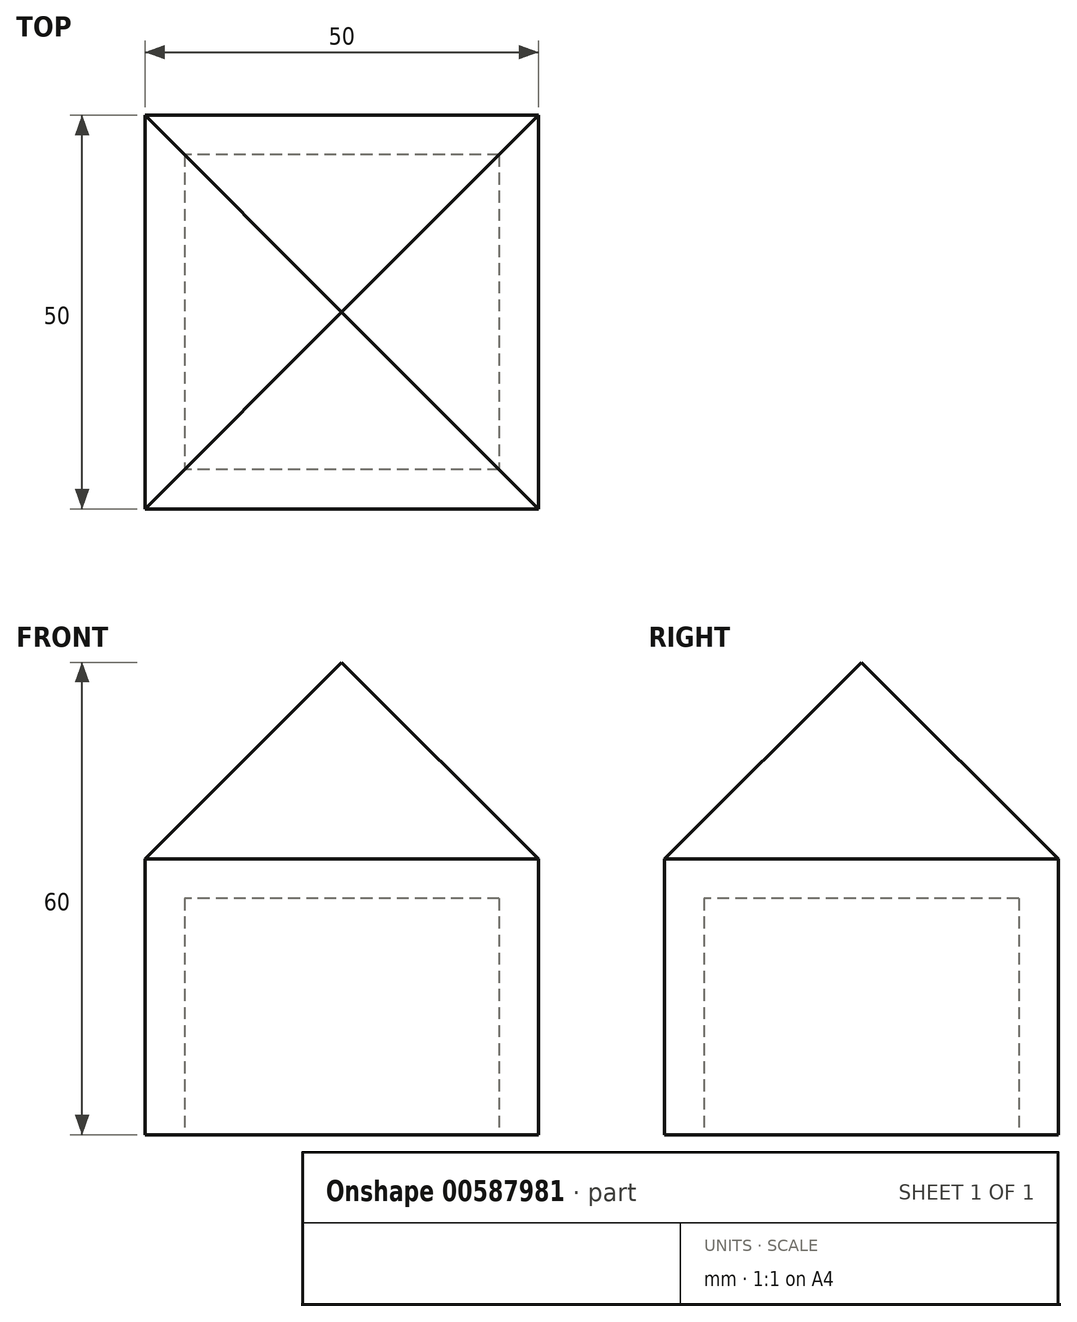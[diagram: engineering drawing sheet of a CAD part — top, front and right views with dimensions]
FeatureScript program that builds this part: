
annotation { "Feature Type Name" : "Feature", "Feature Type Description" : "" }
export const myFeature = defineFeature(function(context is Context, id is Id, definition is map)
    precondition{}
    {
        {
            var Q0;
            Q0=qCreatedBy(makeId("Top.planeOp"),FACE);
            var sketch = newSketch(context, id + "F0", { "sketchPlane" : qUnion([Q0])});
            skCircle(sketch, "E0", {"center": v(0, 0) * mm, "radius": 381 * mm});
            skSolve(sketch);
        }
        {
            var Q0;
            Q0=makeQuery(id+"F0.imprint","IMPRINT",FACE,{"disambiguationData":[TD([[makeQuery(id+"F0.imprint","IMPRINT",EDGE,{"derivedFrom":sQuery(id+"F0.wireOp",EDGE,"E0")}),1.0]])]});
            extrude(context, id + "F1", {"entities" : qUnion([Q0]), "depth" : 762 * mm, "offsetDistance" : 25.4 * mm});
        }
        {
            var Q0;
            Q0=makeQuery(id+"F1.opExtrude","SWEPT_BODY",BODY,{"disambiguationData":[OSD([sQuery(id+"F0.wireOp",EDGE,"E0")])]});
            deleteBodies(context, id + "F2", {"entities" : qUnion([Q0])});
        }
        {
            var Q0;
            Q0=qCreatedBy(makeId("Top.planeOp"),FACE);
            var sketch = newSketch(context, id + "F3", { "sketchPlane" : qUnion([Q0])});
            skLineSegment(sketch, "E1.bottom", {"start": v(25, 25) * mm, "end": v(-25, 25) * mm});
            skLineSegment(sketch, "E1.top", {"start": v(25, -25) * mm, "end": v(-25, -25) * mm});
            skLineSegment(sketch, "E1.left", {"start": v(25, 25) * mm, "end": v(25, -25) * mm});
            skLineSegment(sketch, "E1.right", {"start": v(-25, 25) * mm, "end": v(-25, -25) * mm});
            skPoint(sketch, "E1.middle", {"position": v(0, 0) * mm});
            skLineSegment(sketch, "E2.bottom", {"start": v(20, 20) * mm, "end": v(-20, 20) * mm});
            skLineSegment(sketch, "E2.top", {"start": v(20, -20) * mm, "end": v(-20, -20) * mm});
            skLineSegment(sketch, "E2.left", {"start": v(20, 20) * mm, "end": v(20, -20) * mm});
            skLineSegment(sketch, "E2.right", {"start": v(-20, 20) * mm, "end": v(-20, -20) * mm});
            skSolve(sketch);
        }
        {
            var Q0;
            Q0=makeQuery(id+"F3.imprint","IMPRINT",FACE,{"disambiguationData":[TD([[makeQuery(id+"F3.imprint","IMPRINT",EDGE,{"derivedFrom":sQuery(id+"F3.wireOp",EDGE,"E1.bottom")}),1.0]])]});
            extrude(context, id + "F4", {"entities" : qUnion([Q0]), "depth" : 30 * mm, "offsetDistance" : 25 * mm});
        }
        {
            var Q0;
            Q0=makeQuery(id+"F4.opExtrude","CAP_FACE",FACE,{"disambiguationData":[OSD([sQuery(id+"F3.wireOp",EDGE,"E1.bottom"),sQuery(id+"F3.wireOp",EDGE,"E1.top"),sQuery(id+"F3.wireOp",EDGE,"E1.left"),sQuery(id+"F3.wireOp",EDGE,"E1.right"),sQuery(id+"F3.wireOp",EDGE,"E2.bottom"),sQuery(id+"F3.wireOp",EDGE,"E2.top"),sQuery(id+"F3.wireOp",EDGE,"E2.left"),sQuery(id+"F3.wireOp",EDGE,"E2.right")])],"isStart":false});
            var sketch = newSketch(context, id + "F5", { "sketchPlane" : qUnion([Q0])});
            skLineSegment(sketch, "E3.bottom", {"start": v(25, 25) * mm, "end": v(-25, 25) * mm});
            skLineSegment(sketch, "E3.top", {"start": v(25, -25) * mm, "end": v(-25, -25) * mm});
            skLineSegment(sketch, "E3.left", {"start": v(25, 25) * mm, "end": v(25, -25) * mm});
            skLineSegment(sketch, "E3.right", {"start": v(-25, 25) * mm, "end": v(-25, -25) * mm});
            skPoint(sketch, "E3.middle", {"position": v(0, 0) * mm});
            skSolve(sketch);
        }
        {
            var Q0;
            Q0=makeQuery(id+"F5.imprint","IMPRINT",FACE,{"disambiguationData":[TD([[makeQuery(id+"F5.imprint","IMPRINT",EDGE,{"derivedFrom":makeQuery(id+"F4.opExtrude","CAP_EDGE",EDGE,{"disambiguationData":[OSD([sQuery(id+"F3.wireOp",EDGE,"E2.bottom")])],"isStart":false})}),1.0]])]});
            var Q1;
            Q1=makeQuery(id+"F5.imprint","IMPRINT",FACE,{"disambiguationData":[TD([[makeQuery(id+"F5.imprint","IMPRINT",EDGE,{"derivedFrom":sQuery(id+"F5.wireOp",EDGE,"E3.bottom")}),1.0]])]});
            extrude(context, id + "F6", {"entities" : qUnion([Q0, Q1]), "operationType" : NewBodyOperationType.ADD, "depth" : 30 * mm, "offsetDistance" : 25 * mm});
        }
        {
            var Q0;
            Q0=makeQuery(id+"F6.opExtrude","CAP_FACE",FACE,{"disambiguationData":[OSD([sQuery(id+"F5.wireOp",EDGE,"E3.bottom"),sQuery(id+"F5.wireOp",EDGE,"E3.top"),sQuery(id+"F5.wireOp",EDGE,"E3.left"),sQuery(id+"F5.wireOp",EDGE,"E3.right")])],"isStart":false});
            chamfer(context, id + "F7", {"entities" : qUnion([Q0]), "width" : 25 * mm});
        }
    });
